# Revit family: Faucet-Kitchen-KOHLER-Karbon-K-6227
name_source: partatom
category: Plumbing Fixtures
revit_build: Autodesk Revit 2015 (Build: 20140606_1530(x64)
units: mm (PartAtom-declared; Revit-internal decimal feet)

## types (5) — shared parameters
ADA Compliant = Yes
Assembly Code = D2010
CW Connection = Yes
Cold Water Inlet = Cold Water Inlet
Date Modified = 01/14/2019
Default Elevation = 36"
Drain Included = No
Flow Rate = 2 GPM
HW Connection = Yes
Height = 8 15/16"
Hot Water Inlet = Hot Water Inlet
Length = 13 1/4"
Manufacturer = KOHLER Co.
MasterFormat 1995 = 15410
MasterFormat 2004 = 22.41.39
Material = Premium Metal and Carbon Fiber Construction
Pressure = 60.00 psi
Product Documentation Link = http://www.us.kohler.com
Product Name = Karbon
Product Page URL = http://www.us.kohler.com
Spout Reach = 13 1/4"
URL = https://www.us.kohler.com
Vent Connection = No
Waste Connection = No
Waste Water Outlet = Waste Water Outlet
Width = 2 5/8"

## per-type parameters (varying)
| type | Description | Finish | Model | Tube_Material | Type |
| Silver tube,CP-Polished Chrome | Articulating two-hole deck-mount kitchen sink faucet with 13 inch spout with Silver tube | Kohler-Metal-CP-Polished_Chrome | K-6227-C11-CP | Kohler-Fiber-C11-Silver | 1 |
| Silver tube,VS-Vibrant Stainless | Articulating two-hole deck-mount kitchen sink faucet with 13 inch spout with Silver tube | Kohler-Metal-VS-Vibrant_Stainless | K-6227-C11-VS | Kohler-Fiber-C11-Silver | 2 |
| Black tube,CP-Polished Chrome | Articulating two-hole deck-mount kitchen sink faucet with 13 inch spout with Black tube | Kohler-Metal-CP-Polished_Chrome | K-6227-C12-CP | Kohler-Fiber-C12-Black_Black | 3 |
| Black tube,VS-Vibrant Stainless | Articulating two-hole deck-mount kitchen sink faucet with 13 inch spout with Black tube | Kohler-Metal-VS-Vibrant_Stainless | K-6227-C12-VS | Kohler-Fiber-C12-Black_Black | 4 |
| Bronze tube,BV-Vibrant Brushed Bronze | Articulating two-hole deck-mount kitchen sink faucet with 13 inch spout with Bronze tube | Kohler-Metal-BV-Brushed_Bronze | K-6227-C15-BV | Kohler-Fiber-C15-Brushed_Bronze | 5 |

## geometry (parser evidence)
native form markers: Sweep x8
no freeform markers — native parametric forms only
